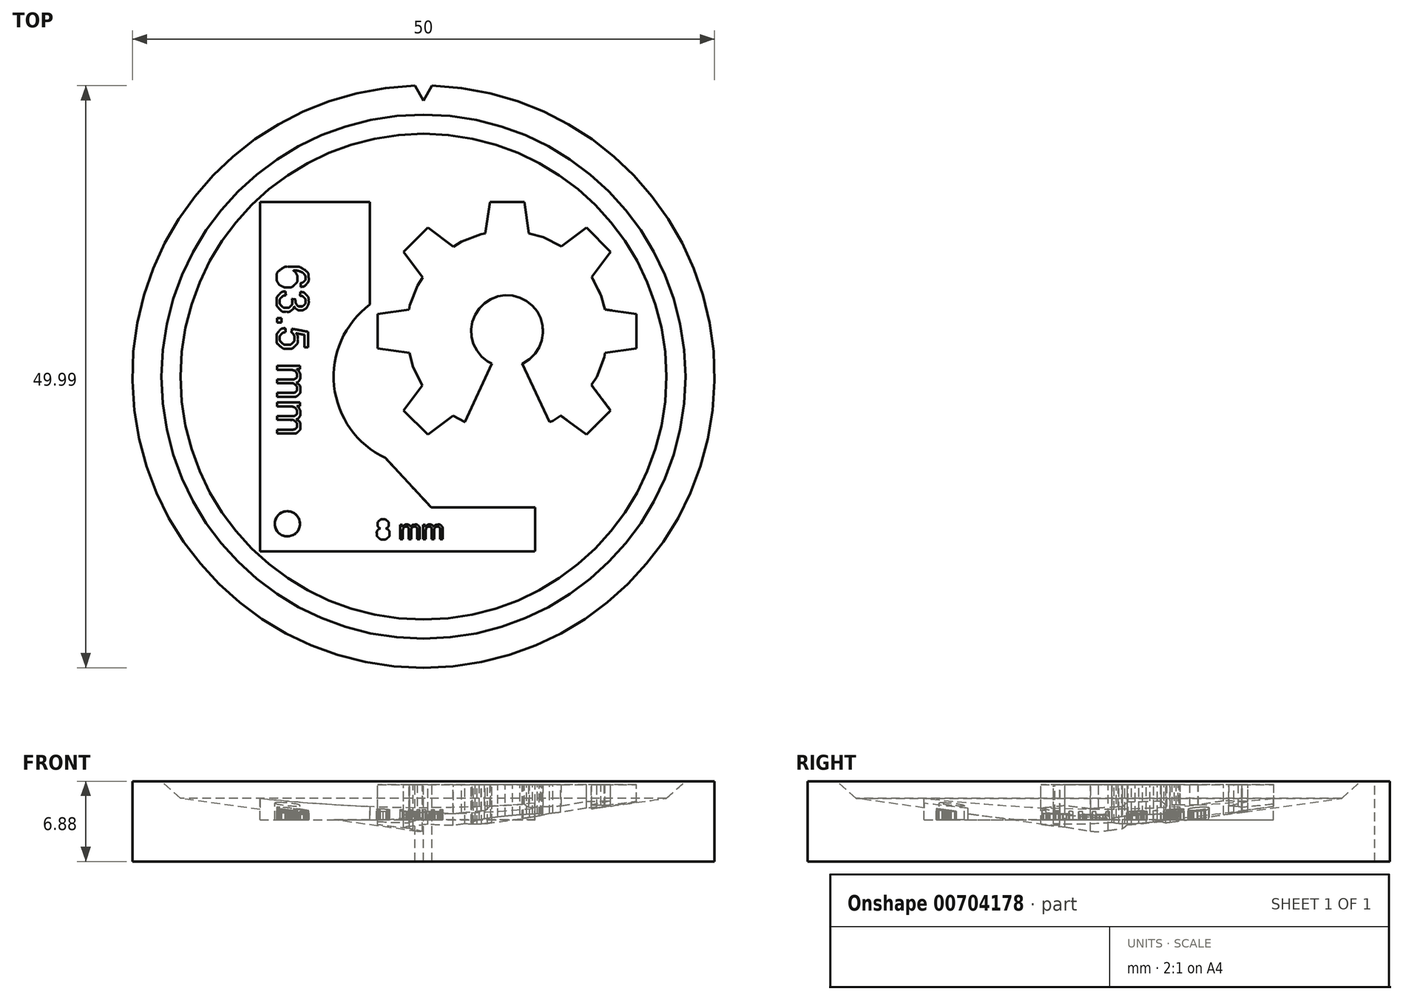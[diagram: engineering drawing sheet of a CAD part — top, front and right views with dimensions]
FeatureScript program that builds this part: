
annotation { "Feature Type Name" : "Feature", "Feature Type Description" : "" }
export const myFeature = defineFeature(function(context is Context, id is Id, definition is map)
    precondition{}
    {
        {
            var Q0;
            Q0=qCreatedBy(makeId("Front.planeOp"),FACE);
            var sketch = newSketch(context, id + "F0", { "sketchPlane" : qUnion([Q0])});
            skLineSegment(sketch, "E0", {"start": v(0, 0) * mm, "end": v(-25, 0) * mm});
            skLineSegment(sketch, "E1", {"start": v(-25, 0) * mm, "end": v(-25, 6.88) * mm});
            skLineSegment(sketch, "E2", {"start": v(-25, 6.88) * mm, "end": v(-22.5, 6.88) * mm});
            skLineSegment(sketch, "E3", {"start": v(-22.5, 6.88) * mm, "end": v(-20.86, 5.42) * mm});
            skLineSegment(sketch, "E4", {"start": v(-20.86, 5.42) * mm, "end": v(0, 2.5) * mm});
            skLineSegment(sketch, "E5", {"start": v(0, 2.5) * mm, "end": v(0, 0) * mm});
            skSolve(sketch);
        }
        {
            var Q0;
            Q0 = qSketchRegion(id + "F0", true);
            var Q1;
            Q1=sQuery(id+"F0.wireOp",EDGE,"E5");
            revolve(context, id + "F1", {"surfaceOperationType" : NewSurfaceOperationType.NEW, "entities" : qUnion([Q0]), "axis" : qUnion([Q1]), "revolveType" : RevolveType.FULL});
        }
        {
            var Q0;
            Q0=makeQuery(id+"F1.opRevolve","SWEPT_FACE",FACE,{"disambiguationData":[OSD([sQuery(id+"F0.wireOp",EDGE,"E2")])]});
            cPlane(context, id + "F2", {"entities" : qUnion([Q0]), "cplaneType" : CPlaneType.OFFSET, "offset" : 25 * mm, "width" : 150 * mm, "height" : 150 * mm});
        }
        {
            var Q0;
            Q0=qCreatedBy(id+"F2.planeOp",FACE);
            var sketch = newSketch(context, id + "F3", { "sketchPlane" : qUnion([Q0])});
            skCircle(sketch, "E6.cCircle", {"center": v(0, 25.35) * mm, "radius": 0.82 * mm, "construction": true});
            skLineSegment(sketch, "E6.0", {"start": v(-1.43, 26.17) * mm, "end": v(1.43, 26.17) * mm});
            skLineSegment(sketch, "E6.1", {"start": v(1.43, 26.17) * mm, "end": v(0, 23.7) * mm});
            skLineSegment(sketch, "E6.2", {"start": v(0, 23.7) * mm, "end": v(-1.43, 26.17) * mm});
            skPoint(sketch, "E6.0.midPoint", {"position": v(0, 26.17) * mm});
            skSolve(sketch);
        }
        {
            var Q0;
            Q0 = qSketchRegion(id + "F3", true);
            extrude(context, id + "F4", {"entities" : qUnion([Q0]), "operationType" : NewBodyOperationType.REMOVE, "oppositeDirection" : true, "depth" : 64 * mm, "offsetDistance" : 25 * mm});
        }
        {
            var Q0;
            Q0=qCreatedBy(id+"F2.planeOp",FACE);
            var sketch = newSketch(context, id + "F5", { "sketchPlane" : qUnion([Q0])});
            skLineSegment(sketch, "E7", {"start": v(-14.05, -15) * mm, "end": v(-14.05, 15) * mm});
            skLineSegment(sketch, "E8", {"start": v(-14.05, 15) * mm, "end": v(-4.6, 15) * mm});
            skLineSegment(sketch, "E9", {"start": v(-14.05, -15) * mm, "end": v(9.57, -15) * mm});
            skLineSegment(sketch, "E10", {"start": v(9.57, -15) * mm, "end": v(9.6, -11.22) * mm});
            skLineSegment(sketch, "E11", {"start": v(9.6, -11.22) * mm, "end": v(0.66, -11.22) * mm});
            skLineSegment(sketch, "E12", {"start": v(-4.6, -5.55) * mm, "end": v(-4.6, 15) * mm});
            skLineSegment(sketch, "E13", {"start": v(0.66, -11.22) * mm, "end": v(-4.6, -5.55) * mm});
            skCircle(sketch, "E14", {"center": v(-11.69, -12.64) * mm, "radius": 1.08 * mm});
            skLineSegment(sketch, "E15", {"start": v(-10.53, 7.7) * mm, "end": v(-10.56, 8.04) * mm});
            skLineSegment(sketch, "E16", {"start": v(-11.86, 7.33) * mm, "end": v(-11.81, 7) * mm});
            skLineSegment(sketch, "E17", {"start": v(-11.3, 6.67) * mm, "end": v(-11, 6.63) * mm});
            skLineSegment(sketch, "E18", {"start": v(-10.62, 6.96) * mm, "end": v(-10.56, 7.3) * mm});
            skLineSegment(sketch, "E19", {"start": v(-12.2, 5.04) * mm, "end": v(-12.57, 5.04) * mm});
            skLineSegment(sketch, "E20", {"start": v(-12.57, 5.04) * mm, "end": v(-12.57, 4.66) * mm});
            skLineSegment(sketch, "E21", {"start": v(-12.57, 4.66) * mm, "end": v(-12.2, 4.66) * mm});
            skLineSegment(sketch, "E22", {"start": v(-12.2, 4.66) * mm, "end": v(-12.2, 5.04) * mm});
            skLineSegment(sketch, "E23", {"start": v(-11.86, 4.17) * mm, "end": v(-11.83, 3.83) * mm});
            skLineSegment(sketch, "E24", {"start": v(-11.33, 3.8) * mm, "end": v(-11.3, 4.12) * mm});
            skLineSegment(sketch, "E25", {"start": v(-11.3, 4.12) * mm, "end": v(-9.9, 3.85) * mm});
            skLineSegment(sketch, "E26", {"start": v(-9.9, 3.85) * mm, "end": v(-9.9, 2.5) * mm});
            skLineSegment(sketch, "E27", {"start": v(-9.9, 2.5) * mm, "end": v(-10.22, 2.5) * mm});
            skLineSegment(sketch, "E28", {"start": v(-10.22, 2.5) * mm, "end": v(-10.22, 3.59) * mm});
            skLineSegment(sketch, "E29", {"start": v(-10.22, 3.59) * mm, "end": v(-10.95, 3.73) * mm});
            skLineSegment(sketch, "E30", {"start": v(-12.57, 0.93) * mm, "end": v(-10.61, 0.93) * mm});
            skLineSegment(sketch, "E31", {"start": v(-10.61, 0.93) * mm, "end": v(-10.61, 0.63) * mm});
            skLineSegment(sketch, "E32", {"start": v(-10.61, 0.63) * mm, "end": v(-10.89, 0.63) * mm});
            skLineSegment(sketch, "E33", {"start": v(-11.23, -1.73) * mm, "end": v(-12.57, -1.73) * mm});
            skLineSegment(sketch, "E34", {"start": v(-12.57, -1.73) * mm, "end": v(-12.57, -1.4) * mm});
            skLineSegment(sketch, "E35", {"start": v(-12.57, -1.4) * mm, "end": v(-11.34, -1.4) * mm});
            skLineSegment(sketch, "E36", {"start": v(-11.43, -0.57) * mm, "end": v(-12.57, -0.57) * mm});
            skLineSegment(sketch, "E37", {"start": v(-12.57, -0.57) * mm, "end": v(-12.57, -0.23) * mm});
            skLineSegment(sketch, "E38", {"start": v(-12.57, -0.23) * mm, "end": v(-11.3, -0.23) * mm});
            skLineSegment(sketch, "E39", {"start": v(-11.56, 0.6) * mm, "end": v(-12.57, 0.6) * mm});
            skLineSegment(sketch, "E40", {"start": v(-12.57, 0.6) * mm, "end": v(-12.57, 0.93) * mm});
            skLineSegment(sketch, "E41", {"start": v(-12.57, -2.22) * mm, "end": v(-10.61, -2.22) * mm});
            skLineSegment(sketch, "E42", {"start": v(-10.61, -2.22) * mm, "end": v(-10.61, -2.51) * mm});
            skLineSegment(sketch, "E43", {"start": v(-10.61, -2.51) * mm, "end": v(-10.89, -2.51) * mm});
            skLineSegment(sketch, "E44", {"start": v(-11.23, -4.87) * mm, "end": v(-12.57, -4.87) * mm});
            skLineSegment(sketch, "E45", {"start": v(-12.57, -4.87) * mm, "end": v(-12.57, -4.54) * mm});
            skLineSegment(sketch, "E46", {"start": v(-12.57, -4.54) * mm, "end": v(-11.34, -4.54) * mm});
            skLineSegment(sketch, "E47", {"start": v(-11.43, -3.71) * mm, "end": v(-12.57, -3.71) * mm});
            skLineSegment(sketch, "E48", {"start": v(-12.57, -3.71) * mm, "end": v(-12.57, -3.38) * mm});
            skLineSegment(sketch, "E49", {"start": v(-12.57, -3.38) * mm, "end": v(-11.3, -3.38) * mm});
            skLineSegment(sketch, "E50", {"start": v(-11.56, -2.55) * mm, "end": v(-12.57, -2.55) * mm});
            skLineSegment(sketch, "E51", {"start": v(-12.57, -2.55) * mm, "end": v(-12.57, -2.22) * mm});
            skFitSpline(sketch, "E52", {"points": [v(-10.56, 8.04) * mm, v(-10.5, 8.05) * mm, v(-10.4, 8.07) * mm, v(-10.3, 8.13) * mm, v(-10.27, 8.16) * mm]});
            skFitSpline(sketch, "E53", {"points": [v(-10.27, 8.16) * mm, v(-10.23, 8.2) * mm, v(-10.15, 8.3) * mm, v(-10.14, 8.43) * mm, v(-10.13, 8.5) * mm]});
            skFitSpline(sketch, "E54", {"points": [v(-10.13, 8.5) * mm, v(-10.13, 8.54) * mm, v(-10.14, 8.64) * mm, v(-10.2, 8.73) * mm, v(-10.22, 8.77) * mm]});
            skFitSpline(sketch, "E55", {"points": [v(-10.22, 8.77) * mm, v(-10.26, 8.82) * mm, v(-10.36, 8.93) * mm, v(-10.48, 8.99) * mm, v(-10.55, 9.02) * mm]});
            skFitSpline(sketch, "E56", {"points": [v(-10.55, 9.02) * mm, v(-10.64, 9.05) * mm, v(-10.84, 9.1) * mm, v(-11.06, 9.11) * mm, v(-11.18, 9.11) * mm]});
            skFitSpline(sketch, "E57", {"points": [v(-11.18, 9.11) * mm, v(-11.12, 9.07) * mm, v(-11.01, 9) * mm, v(-10.94, 8.88) * mm, v(-10.9, 8.82) * mm]});
            skFitSpline(sketch, "E58", {"points": [v(-10.9, 8.82) * mm, v(-10.88, 8.76) * mm, v(-10.83, 8.65) * mm, v(-10.82, 8.52) * mm, v(-10.82, 8.46) * mm]});
            skFitSpline(sketch, "E59", {"points": [v(-10.82, 8.46) * mm, v(-10.83, 8.35) * mm, v(-10.85, 8.13) * mm, v(-11, 7.97) * mm, v(-11.06, 7.9) * mm]});
            skFitSpline(sketch, "E60", {"points": [v(-11.06, 7.9) * mm, v(-11.15, 7.82) * mm, v(-11.34, 7.68) * mm, v(-11.57, 7.67) * mm, v(-11.7, 7.66) * mm]});
            skFitSpline(sketch, "E61", {"points": [v(-11.7, 7.66) * mm, v(-11.78, 7.66) * mm, v(-11.94, 7.67) * mm, v(-12.1, 7.74) * mm, v(-12.17, 7.77) * mm]});
            skFitSpline(sketch, "E62", {"points": [v(-12.17, 7.77) * mm, v(-12.24, 7.8) * mm, v(-12.37, 7.88) * mm, v(-12.46, 8) * mm, v(-12.5, 8.07) * mm]});
            skFitSpline(sketch, "E63", {"points": [v(-12.5, 8.07) * mm, v(-12.54, 8.14) * mm, v(-12.6, 8.27) * mm, v(-12.61, 8.43) * mm, v(-12.62, 8.5) * mm]});
            skFitSpline(sketch, "E64", {"points": [v(-12.62, 8.5) * mm, v(-12.6, 8.64) * mm, v(-12.58, 8.9) * mm, v(-12.4, 9.09) * mm, v(-12.31, 9.18) * mm]});
            skFitSpline(sketch, "E65", {"points": [v(-12.31, 9.18) * mm, v(-12.18, 9.26) * mm, v(-11.87, 9.44) * mm, v(-11.51, 9.44) * mm, v(-11.3, 9.44) * mm]});
            skFitSpline(sketch, "E66", {"points": [v(-11.3, 9.44) * mm, v(-11.08, 9.44) * mm, v(-10.67, 9.43) * mm, v(-10.32, 9.24) * mm, v(-10.17, 9.15) * mm]});
            skFitSpline(sketch, "E67", {"points": [v(-10.17, 9.15) * mm, v(-10.08, 9.06) * mm, v(-9.9, 8.87) * mm, v(-9.87, 8.6) * mm, v(-9.86, 8.47) * mm]});
            skFitSpline(sketch, "E68", {"points": [v(-9.86, 8.47) * mm, v(-9.86, 8.37) * mm, v(-9.87, 8.18) * mm, v(-9.98, 8.02) * mm, v(-10.04, 7.95) * mm]});
            skFitSpline(sketch, "E69", {"points": [v(-10.04, 7.95) * mm, v(-10.1, 7.89) * mm, v(-10.24, 7.76) * mm, v(-10.43, 7.72) * mm, v(-10.53, 7.7) * mm]});
            skFitSpline(sketch, "E70", {"points": [v(-11.7, 9.06) * mm, v(-11.75, 9.06) * mm, v(-11.87, 9.05) * mm, v(-11.97, 9.01) * mm, v(-12.02, 8.99) * mm]});
            skFitSpline(sketch, "E71", {"points": [v(-12.02, 8.99) * mm, v(-12.07, 8.96) * mm, v(-12.17, 8.91) * mm, v(-12.23, 8.83) * mm, v(-12.26, 8.78) * mm]});
            skFitSpline(sketch, "E72", {"points": [v(-12.26, 8.78) * mm, v(-12.29, 8.74) * mm, v(-12.33, 8.66) * mm, v(-12.34, 8.56) * mm, v(-12.35, 8.5) * mm]});
            skFitSpline(sketch, "E73", {"points": [v(-12.35, 8.5) * mm, v(-12.34, 8.44) * mm, v(-12.32, 8.3) * mm, v(-12.23, 8.2) * mm, v(-12.18, 8.15) * mm]});
            skFitSpline(sketch, "E74", {"points": [v(-12.18, 8.15) * mm, v(-12.11, 8.1) * mm, v(-11.97, 8) * mm, v(-11.8, 8) * mm, v(-11.71, 8) * mm]});
            skFitSpline(sketch, "E75", {"points": [v(-11.71, 8) * mm, v(-11.63, 8) * mm, v(-11.47, 8) * mm, v(-11.33, 8.1) * mm, v(-11.27, 8.15) * mm]});
            skFitSpline(sketch, "E76", {"points": [v(-11.27, 8.15) * mm, v(-11.23, 8.2) * mm, v(-11.13, 8.3) * mm, v(-11.12, 8.45) * mm, v(-11.11, 8.52) * mm]});
            skFitSpline(sketch, "E77", {"points": [v(-11.11, 8.52) * mm, v(-11.12, 8.6) * mm, v(-11.13, 8.74) * mm, v(-11.23, 8.85) * mm, v(-11.27, 8.9) * mm]});
            skFitSpline(sketch, "E78", {"points": [v(-11.27, 8.9) * mm, v(-11.33, 8.95) * mm, v(-11.46, 9.05) * mm, v(-11.61, 9.06) * mm, v(-11.7, 9.06) * mm]});
            skFitSpline(sketch, "E79", {"points": [v(-11.81, 7) * mm, v(-11.9, 6.97) * mm, v(-12.05, 6.94) * mm, v(-12.17, 6.84) * mm, v(-12.22, 6.8) * mm]});
            skFitSpline(sketch, "E80", {"points": [v(-12.22, 6.8) * mm, v(-12.26, 6.75) * mm, v(-12.33, 6.65) * mm, v(-12.34, 6.53) * mm, v(-12.35, 6.46) * mm]});
            skFitSpline(sketch, "E81", {"points": [v(-12.35, 6.46) * mm, v(-12.34, 6.39) * mm, v(-12.33, 6.24) * mm, v(-12.23, 6.12) * mm, v(-12.18, 6.07) * mm]});
            skFitSpline(sketch, "E82", {"points": [v(-12.18, 6.07) * mm, v(-12.13, 6.02) * mm, v(-12, 5.92) * mm, v(-11.86, 5.91) * mm, v(-11.78, 5.9) * mm]});
            skFitSpline(sketch, "E83", {"points": [v(-11.78, 5.9) * mm, v(-11.7, 5.91) * mm, v(-11.57, 5.92) * mm, v(-11.46, 6.01) * mm, v(-11.4, 6.06) * mm]});
            skFitSpline(sketch, "E84", {"points": [v(-11.4, 6.06) * mm, v(-11.36, 6.1) * mm, v(-11.27, 6.22) * mm, v(-11.26, 6.36) * mm, v(-11.26, 6.44) * mm]});
            skFitSpline(sketch, "E85", {"points": [v(-11.26, 6.44) * mm, v(-11.26, 6.47) * mm, v(-11.26, 6.55) * mm, v(-11.28, 6.63) * mm, v(-11.3, 6.67) * mm]});
            skFitSpline(sketch, "E86", {"points": [v(-11, 6.63) * mm, v(-11, 6.62) * mm, v(-11, 6.6) * mm, v(-11, 6.59) * mm, v(-11, 6.58) * mm]});
            skFitSpline(sketch, "E87", {"points": [v(-11, 6.58) * mm, v(-11, 6.51) * mm, v(-11, 6.38) * mm, v(-10.93, 6.26) * mm, v(-10.9, 6.2) * mm]});
            skFitSpline(sketch, "E88", {"points": [v(-10.9, 6.2) * mm, v(-10.85, 6.15) * mm, v(-10.76, 6.05) * mm, v(-10.62, 6.03) * mm, v(-10.55, 6.03) * mm]});
            skFitSpline(sketch, "E89", {"points": [v(-10.55, 6.03) * mm, v(-10.5, 6.03) * mm, v(-10.38, 6.04) * mm, v(-10.3, 6.12) * mm, v(-10.25, 6.15) * mm]});
            skFitSpline(sketch, "E90", {"points": [v(-10.25, 6.15) * mm, v(-10.21, 6.2) * mm, v(-10.14, 6.3) * mm, v(-10.13, 6.4) * mm, v(-10.13, 6.47) * mm]});
            skFitSpline(sketch, "E91", {"points": [v(-10.13, 6.47) * mm, v(-10.13, 6.53) * mm, v(-10.14, 6.65) * mm, v(-10.22, 6.75) * mm, v(-10.25, 6.8) * mm]});
            skFitSpline(sketch, "E92", {"points": [v(-10.25, 6.8) * mm, v(-10.3, 6.83) * mm, v(-10.4, 6.92) * mm, v(-10.54, 6.95) * mm, v(-10.62, 6.96) * mm]});
            skFitSpline(sketch, "E93", {"points": [v(-10.56, 7.3) * mm, v(-10.45, 7.27) * mm, v(-10.26, 7.22) * mm, v(-10.1, 7.08) * mm, v(-10.04, 7.02) * mm]});
            skFitSpline(sketch, "E94", {"points": [v(-10.04, 7.02) * mm, v(-9.99, 6.94) * mm, v(-9.88, 6.78) * mm, v(-9.86, 6.58) * mm, v(-9.86, 6.48) * mm]});
            skFitSpline(sketch, "E95", {"points": [v(-9.86, 6.48) * mm, v(-9.86, 6.4) * mm, v(-9.87, 6.26) * mm, v(-9.92, 6.13) * mm, v(-9.95, 6.07) * mm]});
            skFitSpline(sketch, "E96", {"points": [v(-9.95, 6.07) * mm, v(-9.99, 6.01) * mm, v(-10.05, 5.9) * mm, v(-10.16, 5.82) * mm, v(-10.21, 5.79) * mm]});
            skFitSpline(sketch, "E97", {"points": [v(-10.21, 5.79) * mm, v(-10.27, 5.76) * mm, v(-10.38, 5.7) * mm, v(-10.5, 5.7) * mm, v(-10.56, 5.69) * mm]});
            skFitSpline(sketch, "E98", {"points": [v(-10.56, 5.69) * mm, v(-10.62, 5.7) * mm, v(-10.73, 5.7) * mm, v(-10.83, 5.75) * mm, v(-10.88, 5.78) * mm]});
            skFitSpline(sketch, "E99", {"points": [v(-10.88, 5.78) * mm, v(-10.92, 5.82) * mm, v(-11.02, 5.9) * mm, v(-11.08, 6) * mm, v(-11.1, 6.06) * mm]});
            skFitSpline(sketch, "E100", {"points": [v(-11.1, 6.06) * mm, v(-11.13, 5.98) * mm, v(-11.17, 5.84) * mm, v(-11.28, 5.74) * mm, v(-11.34, 5.69) * mm]});
            skFitSpline(sketch, "E101", {"points": [v(-11.34, 5.69) * mm, v(-11.4, 5.65) * mm, v(-11.53, 5.57) * mm, v(-11.7, 5.56) * mm, v(-11.77, 5.55) * mm]});
            skFitSpline(sketch, "E102", {"points": [v(-11.77, 5.55) * mm, v(-11.89, 5.56) * mm, v(-12.12, 5.59) * mm, v(-12.29, 5.74) * mm, v(-12.37, 5.81) * mm]});
            skFitSpline(sketch, "E103", {"points": [v(-12.37, 5.81) * mm, v(-12.45, 5.9) * mm, v(-12.6, 6.1) * mm, v(-12.61, 6.34) * mm, v(-12.62, 6.47) * mm]});
            skFitSpline(sketch, "E104", {"points": [v(-12.62, 6.47) * mm, v(-12.61, 6.58) * mm, v(-12.6, 6.8) * mm, v(-12.47, 6.97) * mm, v(-12.4, 7.06) * mm]});
            skFitSpline(sketch, "E105", {"points": [v(-12.4, 7.06) * mm, v(-12.33, 7.13) * mm, v(-12.17, 7.27) * mm, v(-11.97, 7.3) * mm, v(-11.86, 7.33) * mm]});
            skFitSpline(sketch, "E106", {"points": [v(-11.83, 3.83) * mm, v(-11.91, 3.81) * mm, v(-12.06, 3.78) * mm, v(-12.17, 3.69) * mm, v(-12.22, 3.65) * mm]});
            skFitSpline(sketch, "E107", {"points": [v(-12.22, 3.65) * mm, v(-12.25, 3.6) * mm, v(-12.33, 3.5) * mm, v(-12.34, 3.37) * mm, v(-12.35, 3.3) * mm]});
            skFitSpline(sketch, "E108", {"points": [v(-12.35, 3.3) * mm, v(-12.34, 3.23) * mm, v(-12.32, 3.07) * mm, v(-12.22, 2.96) * mm, v(-12.16, 2.9) * mm]});
            skFitSpline(sketch, "E109", {"points": [v(-12.16, 2.9) * mm, v(-12.1, 2.85) * mm, v(-11.95, 2.75) * mm, v(-11.78, 2.74) * mm, v(-11.69, 2.73) * mm]});
            skFitSpline(sketch, "E110", {"points": [v(-11.69, 2.73) * mm, v(-11.6, 2.74) * mm, v(-11.43, 2.75) * mm, v(-11.3, 2.85) * mm, v(-11.24, 2.9) * mm]});
            skFitSpline(sketch, "E111", {"points": [v(-11.24, 2.9) * mm, v(-11.19, 2.95) * mm, v(-11.09, 3.07) * mm, v(-11.08, 3.23) * mm, v(-11.07, 3.31) * mm]});
            skFitSpline(sketch, "E112", {"points": [v(-11.07, 3.31) * mm, v(-11.08, 3.36) * mm, v(-11.08, 3.46) * mm, v(-11.12, 3.56) * mm, v(-11.15, 3.6) * mm]});
            skFitSpline(sketch, "E113", {"points": [v(-11.15, 3.6) * mm, v(-11.17, 3.64) * mm, v(-11.22, 3.72) * mm, v(-11.3, 3.78) * mm, v(-11.33, 3.8) * mm]});
            skFitSpline(sketch, "E114", {"points": [v(-10.95, 3.73) * mm, v(-10.9, 3.65) * mm, v(-10.8, 3.5) * mm, v(-10.79, 3.31) * mm, v(-10.78, 3.22) * mm]});
            skFitSpline(sketch, "E115", {"points": [v(-10.78, 3.22) * mm, v(-10.79, 3.1) * mm, v(-10.8, 2.88) * mm, v(-10.95, 2.71) * mm, v(-11.02, 2.62) * mm]});
            skFitSpline(sketch, "E116", {"points": [v(-11.02, 2.62) * mm, v(-11.11, 2.55) * mm, v(-11.3, 2.4) * mm, v(-11.53, 2.39) * mm, v(-11.66, 2.38) * mm]});
            skFitSpline(sketch, "E117", {"points": [v(-11.66, 2.38) * mm, v(-11.77, 2.39) * mm, v(-12, 2.4) * mm, v(-12.2, 2.53) * mm, v(-12.3, 2.6) * mm]});
            skFitSpline(sketch, "E118", {"points": [v(-12.3, 2.6) * mm, v(-12.39, 2.7) * mm, v(-12.58, 2.89) * mm, v(-12.6, 3.16) * mm, v(-12.62, 3.3) * mm]});
            skFitSpline(sketch, "E119", {"points": [v(-12.62, 3.3) * mm, v(-12.61, 3.42) * mm, v(-12.6, 3.64) * mm, v(-12.47, 3.82) * mm, v(-12.41, 3.9) * mm]});
            skFitSpline(sketch, "E120", {"points": [v(-12.41, 3.9) * mm, v(-12.34, 3.98) * mm, v(-12.18, 4.12) * mm, v(-11.97, 4.16) * mm, v(-11.86, 4.17) * mm]});
            skFitSpline(sketch, "E121", {"points": [v(-10.89, 0.63) * mm, v(-10.84, 0.6) * mm, v(-10.75, 0.53) * mm, v(-10.69, 0.44) * mm, v(-10.66, 0.39) * mm]});
            skFitSpline(sketch, "E122", {"points": [v(-10.66, 0.39) * mm, v(-10.63, 0.33) * mm, v(-10.58, 0.22) * mm, v(-10.57, 0.1) * mm, v(-10.57, 0.04) * mm]});
            skFitSpline(sketch, "E123", {"points": [v(-10.57, 0.04) * mm, v(-10.57, -0.03) * mm, v(-10.58, -0.15) * mm, v(-10.63, -0.27) * mm, v(-10.66, -0.32) * mm]});
            skFitSpline(sketch, "E124", {"points": [v(-10.66, -0.32) * mm, v(-10.7, -0.36) * mm, v(-10.76, -0.45) * mm, v(-10.86, -0.5) * mm, v(-10.91, -0.51) * mm]});
            skFitSpline(sketch, "E125", {"points": [v(-10.91, -0.51) * mm, v(-10.81, -0.6) * mm, v(-10.62, -0.75) * mm, v(-10.58, -1) * mm, v(-10.57, -1.12) * mm]});
            skFitSpline(sketch, "E126", {"points": [v(-10.57, -1.12) * mm, v(-10.57, -1.2) * mm, v(-10.58, -1.38) * mm, v(-10.68, -1.5) * mm, v(-10.73, -1.57) * mm]});
            skFitSpline(sketch, "E127", {"points": [v(-10.73, -1.57) * mm, v(-10.8, -1.61) * mm, v(-10.94, -1.72) * mm, v(-11.13, -1.72) * mm, v(-11.23, -1.73) * mm]});
            skFitSpline(sketch, "E128", {"points": [v(-11.34, -1.4) * mm, v(-11.28, -1.4) * mm, v(-11.18, -1.4) * mm, v(-11.09, -1.37) * mm, v(-11.05, -1.36) * mm]});
            skFitSpline(sketch, "E129", {"points": [v(-11.05, -1.36) * mm, v(-11.02, -1.35) * mm, v(-10.97, -1.32) * mm, v(-10.93, -1.27) * mm, v(-10.9, -1.25) * mm]});
            skFitSpline(sketch, "E130", {"points": [v(-10.9, -1.25) * mm, v(-10.9, -1.22) * mm, v(-10.86, -1.15) * mm, v(-10.86, -1.08) * mm, v(-10.86, -1.05) * mm]});
            skFitSpline(sketch, "E131", {"points": [v(-10.86, -1.05) * mm, v(-10.86, -0.98) * mm, v(-10.87, -0.85) * mm, v(-10.95, -0.75) * mm, v(-11, -0.7) * mm]});
            skFitSpline(sketch, "E132", {"points": [v(-11, -0.7) * mm, v(-11.05, -0.66) * mm, v(-11.18, -0.57) * mm, v(-11.34, -0.57) * mm, v(-11.43, -0.57) * mm]});
            skFitSpline(sketch, "E133", {"points": [v(-11.3, -0.23) * mm, v(-11.23, -0.23) * mm, v(-11.12, -0.23) * mm, v(-11.01, -0.18) * mm, v(-10.97, -0.15) * mm]});
            skFitSpline(sketch, "E134", {"points": [v(-10.97, -0.15) * mm, v(-10.93, -0.12) * mm, v(-10.86, -0.05) * mm, v(-10.86, 0.06) * mm, v(-10.86, 0.11) * mm]});
            skFitSpline(sketch, "E135", {"points": [v(-10.86, 0.11) * mm, v(-10.86, 0.16) * mm, v(-10.87, 0.25) * mm, v(-10.9, 0.33) * mm, v(-10.93, 0.37) * mm]});
            skFitSpline(sketch, "E136", {"points": [v(-10.93, 0.37) * mm, v(-10.96, 0.4) * mm, v(-11.02, 0.49) * mm, v(-11.1, 0.52) * mm, v(-11.15, 0.54) * mm]});
            skFitSpline(sketch, "E137", {"points": [v(-11.15, 0.54) * mm, v(-11.2, 0.56) * mm, v(-11.34, 0.6) * mm, v(-11.48, 0.6) * mm, v(-11.56, 0.6) * mm]});
            skFitSpline(sketch, "E138", {"points": [v(-10.89, -2.51) * mm, v(-10.84, -2.55) * mm, v(-10.75, -2.62) * mm, v(-10.69, -2.71) * mm, v(-10.66, -2.76) * mm]});
            skFitSpline(sketch, "E139", {"points": [v(-10.66, -2.76) * mm, v(-10.63, -2.81) * mm, v(-10.58, -2.92) * mm, v(-10.57, -3.05) * mm, v(-10.57, -3.1) * mm]});
            skFitSpline(sketch, "E140", {"points": [v(-10.57, -3.1) * mm, v(-10.57, -3.18) * mm, v(-10.58, -3.3) * mm, v(-10.63, -3.41) * mm, v(-10.66, -3.47) * mm]});
            skFitSpline(sketch, "E141", {"points": [v(-10.66, -3.47) * mm, v(-10.7, -3.5) * mm, v(-10.76, -3.6) * mm, v(-10.86, -3.64) * mm, v(-10.91, -3.66) * mm]});
            skFitSpline(sketch, "E142", {"points": [v(-10.91, -3.66) * mm, v(-10.81, -3.74) * mm, v(-10.62, -3.9) * mm, v(-10.58, -4.15) * mm, v(-10.57, -4.27) * mm]});
            skFitSpline(sketch, "E143", {"points": [v(-10.57, -4.27) * mm, v(-10.57, -4.36) * mm, v(-10.58, -4.52) * mm, v(-10.68, -4.66) * mm, v(-10.73, -4.72) * mm]});
            skFitSpline(sketch, "E144", {"points": [v(-10.73, -4.72) * mm, v(-10.8, -4.76) * mm, v(-10.94, -4.86) * mm, v(-11.13, -4.87) * mm, v(-11.23, -4.87) * mm]});
            skFitSpline(sketch, "E145", {"points": [v(-11.34, -4.54) * mm, v(-11.28, -4.54) * mm, v(-11.18, -4.54) * mm, v(-11.09, -4.52) * mm, v(-11.05, -4.51) * mm]});
            skFitSpline(sketch, "E146", {"points": [v(-11.05, -4.51) * mm, v(-11.02, -4.5) * mm, v(-10.97, -4.47) * mm, v(-10.93, -4.42) * mm, v(-10.9, -4.4) * mm]});
            skFitSpline(sketch, "E147", {"points": [v(-10.9, -4.4) * mm, v(-10.9, -4.36) * mm, v(-10.86, -4.3) * mm, v(-10.86, -4.23) * mm, v(-10.86, -4.2) * mm]});
            skFitSpline(sketch, "E148", {"points": [v(-10.86, -4.2) * mm, v(-10.86, -4.13) * mm, v(-10.87, -4) * mm, v(-10.95, -3.9) * mm, v(-11, -3.85) * mm]});
            skFitSpline(sketch, "E149", {"points": [v(-11, -3.85) * mm, v(-11.05, -3.81) * mm, v(-11.18, -3.72) * mm, v(-11.34, -3.72) * mm, v(-11.43, -3.71) * mm]});
            skFitSpline(sketch, "E150", {"points": [v(-11.3, -3.38) * mm, v(-11.23, -3.38) * mm, v(-11.12, -3.38) * mm, v(-11.01, -3.32) * mm, v(-10.97, -3.3) * mm]});
            skFitSpline(sketch, "E151", {"points": [v(-10.97, -3.3) * mm, v(-10.93, -3.27) * mm, v(-10.86, -3.2) * mm, v(-10.86, -3.1) * mm, v(-10.86, -3.04) * mm]});
            skFitSpline(sketch, "E152", {"points": [v(-10.86, -3.04) * mm, v(-10.86, -2.99) * mm, v(-10.87, -2.9) * mm, v(-10.9, -2.82) * mm, v(-10.93, -2.78) * mm]});
            skFitSpline(sketch, "E153", {"points": [v(-10.93, -2.78) * mm, v(-10.96, -2.74) * mm, v(-11.02, -2.66) * mm, v(-11.1, -2.62) * mm, v(-11.15, -2.6) * mm]});
            skFitSpline(sketch, "E154", {"points": [v(-11.15, -2.6) * mm, v(-11.2, -2.59) * mm, v(-11.34, -2.55) * mm, v(-11.48, -2.55) * mm, v(-11.56, -2.55) * mm]});
            skLineSegment(sketch, "E155", {"start": v(-1.99, -13.95) * mm, "end": v(-1.99, -12.72) * mm});
            skLineSegment(sketch, "E156", {"start": v(-1.99, -12.72) * mm, "end": v(-1.8, -12.72) * mm});
            skLineSegment(sketch, "E157", {"start": v(-1.8, -12.72) * mm, "end": v(-1.8, -12.9) * mm});
            skLineSegment(sketch, "E158", {"start": v(-0.33, -13.1) * mm, "end": v(-0.33, -13.95) * mm});
            skLineSegment(sketch, "E159", {"start": v(-0.33, -13.95) * mm, "end": v(-0.54, -13.95) * mm});
            skLineSegment(sketch, "E160", {"start": v(-0.54, -13.95) * mm, "end": v(-0.54, -13.18) * mm});
            skLineSegment(sketch, "E161", {"start": v(-1.05, -13.24) * mm, "end": v(-1.05, -13.95) * mm});
            skLineSegment(sketch, "E162", {"start": v(-1.05, -13.95) * mm, "end": v(-1.26, -13.95) * mm});
            skLineSegment(sketch, "E163", {"start": v(-1.26, -13.95) * mm, "end": v(-1.26, -13.15) * mm});
            skLineSegment(sketch, "E164", {"start": v(-1.78, -13.31) * mm, "end": v(-1.78, -13.95) * mm});
            skLineSegment(sketch, "E165", {"start": v(-1.78, -13.95) * mm, "end": v(-1.99, -13.95) * mm});
            skLineSegment(sketch, "E166", {"start": v(-0.02, -13.95) * mm, "end": v(-0.02, -12.72) * mm});
            skLineSegment(sketch, "E167", {"start": v(-0.02, -12.72) * mm, "end": v(0.16, -12.72) * mm});
            skLineSegment(sketch, "E168", {"start": v(0.16, -12.72) * mm, "end": v(0.16, -12.9) * mm});
            skLineSegment(sketch, "E169", {"start": v(1.64, -13.1) * mm, "end": v(1.64, -13.95) * mm});
            skLineSegment(sketch, "E170", {"start": v(1.64, -13.95) * mm, "end": v(1.43, -13.95) * mm});
            skLineSegment(sketch, "E171", {"start": v(1.43, -13.95) * mm, "end": v(1.43, -13.18) * mm});
            skLineSegment(sketch, "E172", {"start": v(0.91, -13.24) * mm, "end": v(0.91, -13.95) * mm});
            skLineSegment(sketch, "E173", {"start": v(0.91, -13.95) * mm, "end": v(0.7, -13.95) * mm});
            skLineSegment(sketch, "E174", {"start": v(0.7, -13.95) * mm, "end": v(0.7, -13.15) * mm});
            skLineSegment(sketch, "E175", {"start": v(0.19, -13.31) * mm, "end": v(0.19, -13.95) * mm});
            skLineSegment(sketch, "E176", {"start": v(0.19, -13.95) * mm, "end": v(-0.02, -13.95) * mm});
            skFitSpline(sketch, "E177", {"points": [v(-3.7, -13.03) * mm, v(-3.74, -13.02) * mm, v(-3.81, -12.99) * mm, v(-3.86, -12.93) * mm, v(-3.89, -12.9) * mm]});
            skFitSpline(sketch, "E178", {"points": [v(-3.89, -12.9) * mm, v(-3.9, -12.87) * mm, v(-3.94, -12.8) * mm, v(-3.95, -12.73) * mm, v(-3.95, -12.69) * mm]});
            skFitSpline(sketch, "E179", {"points": [v(-3.95, -12.69) * mm, v(-3.94, -12.63) * mm, v(-3.93, -12.51) * mm, v(-3.86, -12.42) * mm, v(-3.82, -12.38) * mm]});
            skFitSpline(sketch, "E180", {"points": [v(-3.82, -12.38) * mm, v(-3.77, -12.34) * mm, v(-3.66, -12.26) * mm, v(-3.53, -12.26) * mm, v(-3.46, -12.25) * mm]});
            skFitSpline(sketch, "E181", {"points": [v(-3.46, -12.25) * mm, v(-3.4, -12.26) * mm, v(-3.26, -12.26) * mm, v(-3.16, -12.34) * mm, v(-3.1, -12.38) * mm]});
            skFitSpline(sketch, "E182", {"points": [v(-3.1, -12.38) * mm, v(-3.07, -12.43) * mm, v(-3, -12.52) * mm, v(-2.98, -12.63) * mm, v(-2.97, -12.7) * mm]});
            skFitSpline(sketch, "E183", {"points": [v(-2.97, -12.7) * mm, v(-2.98, -12.73) * mm, v(-2.98, -12.8) * mm, v(-3.02, -12.87) * mm, v(-3.04, -12.9) * mm]});
            skFitSpline(sketch, "E184", {"points": [v(-3.04, -12.9) * mm, v(-3.06, -12.93) * mm, v(-3.11, -12.99) * mm, v(-3.18, -13.02) * mm, v(-3.22, -13.03) * mm]});
            skFitSpline(sketch, "E185", {"points": [v(-3.22, -13.03) * mm, v(-3.17, -13.05) * mm, v(-3.08, -13.09) * mm, v(-3.02, -13.16) * mm, v(-2.99, -13.2) * mm]});
            skFitSpline(sketch, "E186", {"points": [v(-2.99, -13.2) * mm, v(-2.96, -13.24) * mm, v(-2.91, -13.32) * mm, v(-2.9, -13.42) * mm, v(-2.9, -13.47) * mm]});
            skFitSpline(sketch, "E187", {"points": [v(-2.9, -13.47) * mm, v(-2.91, -13.54) * mm, v(-2.92, -13.67) * mm, v(-3.01, -13.78) * mm, v(-3.06, -13.83) * mm]});
            skFitSpline(sketch, "E188", {"points": [v(-3.06, -13.83) * mm, v(-3.11, -13.87) * mm, v(-3.23, -13.96) * mm, v(-3.38, -13.97) * mm, v(-3.46, -13.98) * mm]});
            skFitSpline(sketch, "E189", {"points": [v(-3.46, -13.98) * mm, v(-3.54, -13.97) * mm, v(-3.69, -13.96) * mm, v(-3.8, -13.87) * mm, v(-3.87, -13.83) * mm]});
            skFitSpline(sketch, "E190", {"points": [v(-3.87, -13.83) * mm, v(-3.9, -13.78) * mm, v(-4, -13.67) * mm, v(-4.01, -13.53) * mm, v(-4.02, -13.46) * mm]});
            skFitSpline(sketch, "E191", {"points": [v(-4.02, -13.46) * mm, v(-4.02, -13.4) * mm, v(-4.01, -13.3) * mm, v(-3.96, -13.22) * mm, v(-3.93, -13.18) * mm]});
            skFitSpline(sketch, "E192", {"points": [v(-3.93, -13.18) * mm, v(-3.9, -13.15) * mm, v(-3.84, -13.08) * mm, v(-3.74, -13.05) * mm, v(-3.7, -13.03) * mm]});
            skFitSpline(sketch, "E193", {"points": [v(-3.74, -12.68) * mm, v(-3.74, -12.72) * mm, v(-3.73, -12.8) * mm, v(-3.68, -12.85) * mm, v(-3.66, -12.88) * mm]});
            skFitSpline(sketch, "E194", {"points": [v(-3.66, -12.88) * mm, v(-3.63, -12.9) * mm, v(-3.57, -12.95) * mm, v(-3.5, -12.95) * mm, v(-3.46, -12.95) * mm]});
            skFitSpline(sketch, "E195", {"points": [v(-3.46, -12.95) * mm, v(-3.42, -12.95) * mm, v(-3.35, -12.95) * mm, v(-3.3, -12.9) * mm, v(-3.26, -12.88) * mm]});
            skFitSpline(sketch, "E196", {"points": [v(-3.26, -12.88) * mm, v(-3.24, -12.85) * mm, v(-3.2, -12.8) * mm, v(-3.2, -12.73) * mm, v(-3.19, -12.7) * mm]});
            skFitSpline(sketch, "E197", {"points": [v(-3.19, -12.7) * mm, v(-3.2, -12.66) * mm, v(-3.2, -12.58) * mm, v(-3.24, -12.53) * mm, v(-3.27, -12.5) * mm]});
            skFitSpline(sketch, "E198", {"points": [v(-3.27, -12.5) * mm, v(-3.3, -12.48) * mm, v(-3.35, -12.43) * mm, v(-3.43, -12.43) * mm, v(-3.46, -12.42) * mm]});
            skFitSpline(sketch, "E199", {"points": [v(-3.46, -12.42) * mm, v(-3.5, -12.43) * mm, v(-3.57, -12.43) * mm, v(-3.63, -12.48) * mm, v(-3.66, -12.5) * mm]});
            skFitSpline(sketch, "E200", {"points": [v(-3.66, -12.5) * mm, v(-3.68, -12.53) * mm, v(-3.73, -12.58) * mm, v(-3.73, -12.65) * mm, v(-3.74, -12.68) * mm]});
            skFitSpline(sketch, "E201", {"points": [v(-3.8, -13.46) * mm, v(-3.8, -13.5) * mm, v(-3.8, -13.55) * mm, v(-3.78, -13.6) * mm, v(-3.76, -13.63) * mm]});
            skFitSpline(sketch, "E202", {"points": [v(-3.76, -13.63) * mm, v(-3.75, -13.66) * mm, v(-3.72, -13.71) * mm, v(-3.66, -13.75) * mm, v(-3.64, -13.76) * mm]});
            skFitSpline(sketch, "E203", {"points": [v(-3.64, -13.76) * mm, v(-3.6, -13.78) * mm, v(-3.55, -13.8) * mm, v(-3.5, -13.8) * mm, v(-3.46, -13.8) * mm]});
            skFitSpline(sketch, "E204", {"points": [v(-3.46, -13.8) * mm, v(-3.41, -13.8) * mm, v(-3.32, -13.8) * mm, v(-3.25, -13.74) * mm, v(-3.21, -13.71) * mm]});
            skFitSpline(sketch, "E205", {"points": [v(-3.21, -13.71) * mm, v(-3.19, -13.68) * mm, v(-3.13, -13.6) * mm, v(-3.12, -13.52) * mm, v(-3.12, -13.47) * mm]});
            skFitSpline(sketch, "E206", {"points": [v(-3.12, -13.47) * mm, v(-3.12, -13.42) * mm, v(-3.13, -13.33) * mm, v(-3.19, -13.26) * mm, v(-3.22, -13.22) * mm]});
            skFitSpline(sketch, "E207", {"points": [v(-3.22, -13.22) * mm, v(-3.25, -13.2) * mm, v(-3.33, -13.13) * mm, v(-3.42, -13.13) * mm, v(-3.47, -13.12) * mm]});
            skFitSpline(sketch, "E208", {"points": [v(-3.47, -13.12) * mm, v(-3.51, -13.13) * mm, v(-3.6, -13.13) * mm, v(-3.67, -13.2) * mm, v(-3.7, -13.22) * mm]});
            skFitSpline(sketch, "E209", {"points": [v(-3.7, -13.22) * mm, v(-3.74, -13.25) * mm, v(-3.8, -13.33) * mm, v(-3.8, -13.42) * mm, v(-3.8, -13.46) * mm]});
            skFitSpline(sketch, "E210", {"points": [v(-1.8, -12.9) * mm, v(-1.78, -12.87) * mm, v(-1.74, -12.81) * mm, v(-1.68, -12.77) * mm, v(-1.65, -12.75) * mm]});
            skFitSpline(sketch, "E211", {"points": [v(-1.65, -12.75) * mm, v(-1.62, -12.74) * mm, v(-1.55, -12.7) * mm, v(-1.47, -12.7) * mm, v(-1.43, -12.7) * mm]});
            skFitSpline(sketch, "E212", {"points": [v(-1.43, -12.7) * mm, v(-1.39, -12.7) * mm, v(-1.31, -12.7) * mm, v(-1.24, -12.74) * mm, v(-1.2, -12.75) * mm]});
            skFitSpline(sketch, "E213", {"points": [v(-1.2, -12.75) * mm, v(-1.18, -12.77) * mm, v(-1.13, -12.82) * mm, v(-1.1, -12.88) * mm, v(-1.09, -12.91) * mm]});
            skFitSpline(sketch, "E214", {"points": [v(-1.09, -12.91) * mm, v(-1.03, -12.85) * mm, v(-0.94, -12.73) * mm, v(-0.78, -12.7) * mm, v(-0.7, -12.7) * mm]});
            skFitSpline(sketch, "E215", {"points": [v(-0.7, -12.7) * mm, v(-0.65, -12.7) * mm, v(-0.55, -12.7) * mm, v(-0.46, -12.77) * mm, v(-0.43, -12.8) * mm]});
            skFitSpline(sketch, "E216", {"points": [v(-0.43, -12.8) * mm, v(-0.4, -12.84) * mm, v(-0.33, -12.93) * mm, v(-0.33, -13.05) * mm, v(-0.33, -13.1) * mm]});
            skFitSpline(sketch, "E217", {"points": [v(-0.54, -13.18) * mm, v(-0.54, -13.14) * mm, v(-0.54, -13.08) * mm, v(-0.55, -13.02) * mm, v(-0.56, -13) * mm]});
            skFitSpline(sketch, "E218", {"points": [v(-0.56, -13) * mm, v(-0.56, -12.98) * mm, v(-0.58, -12.95) * mm, v(-0.61, -12.92) * mm, v(-0.63, -12.91) * mm]});
            skFitSpline(sketch, "E219", {"points": [v(-0.63, -12.91) * mm, v(-0.65, -12.9) * mm, v(-0.69, -12.88) * mm, v(-0.73, -12.88) * mm, v(-0.75, -12.88) * mm]});
            skFitSpline(sketch, "E220", {"points": [v(-0.75, -12.88) * mm, v(-0.8, -12.88) * mm, v(-0.87, -12.89) * mm, v(-0.94, -12.94) * mm, v(-0.97, -12.96) * mm]});
            skFitSpline(sketch, "E221", {"points": [v(-0.97, -12.96) * mm, v(-1, -13) * mm, v(-1.05, -13.08) * mm, v(-1.05, -13.18) * mm, v(-1.05, -13.24) * mm]});
            skFitSpline(sketch, "E222", {"points": [v(-1.26, -13.15) * mm, v(-1.26, -13.11) * mm, v(-1.26, -13.04) * mm, v(-1.3, -12.97) * mm, v(-1.31, -12.95) * mm]});
            skFitSpline(sketch, "E223", {"points": [v(-1.31, -12.95) * mm, v(-1.33, -12.93) * mm, v(-1.38, -12.88) * mm, v(-1.44, -12.88) * mm, v(-1.48, -12.88) * mm]});
            skFitSpline(sketch, "E224", {"points": [v(-1.48, -12.88) * mm, v(-1.5, -12.88) * mm, v(-1.56, -12.88) * mm, v(-1.61, -12.9) * mm, v(-1.64, -12.92) * mm]});
            skFitSpline(sketch, "E225", {"points": [v(-1.64, -12.92) * mm, v(-1.66, -12.94) * mm, v(-1.71, -12.98) * mm, v(-1.73, -13.03) * mm, v(-1.75, -13.06) * mm]});
            skFitSpline(sketch, "E226", {"points": [v(-1.75, -13.06) * mm, v(-1.76, -13.1) * mm, v(-1.78, -13.18) * mm, v(-1.78, -13.26) * mm, v(-1.78, -13.31) * mm]});
            skFitSpline(sketch, "E227", {"points": [v(0.16, -12.9) * mm, v(0.19, -12.87) * mm, v(0.23, -12.81) * mm, v(0.29, -12.77) * mm, v(0.32, -12.75) * mm]});
            skFitSpline(sketch, "E228", {"points": [v(0.32, -12.75) * mm, v(0.35, -12.74) * mm, v(0.42, -12.7) * mm, v(0.5, -12.7) * mm, v(0.54, -12.7) * mm]});
            skFitSpline(sketch, "E229", {"points": [v(0.54, -12.7) * mm, v(0.58, -12.7) * mm, v(0.66, -12.7) * mm, v(0.73, -12.74) * mm, v(0.76, -12.75) * mm]});
            skFitSpline(sketch, "E230", {"points": [v(0.76, -12.75) * mm, v(0.79, -12.77) * mm, v(0.84, -12.82) * mm, v(0.87, -12.88) * mm, v(0.88, -12.91) * mm]});
            skFitSpline(sketch, "E231", {"points": [v(0.88, -12.91) * mm, v(0.93, -12.85) * mm, v(1.03, -12.73) * mm, v(1.19, -12.7) * mm, v(1.26, -12.7) * mm]});
            skFitSpline(sketch, "E232", {"points": [v(1.26, -12.7) * mm, v(1.32, -12.7) * mm, v(1.42, -12.7) * mm, v(1.5, -12.77) * mm, v(1.54, -12.8) * mm]});
            skFitSpline(sketch, "E233", {"points": [v(1.54, -12.8) * mm, v(1.57, -12.84) * mm, v(1.63, -12.93) * mm, v(1.64, -13.05) * mm, v(1.64, -13.1) * mm]});
            skFitSpline(sketch, "E234", {"points": [v(1.43, -13.18) * mm, v(1.43, -13.14) * mm, v(1.43, -13.08) * mm, v(1.42, -13.02) * mm, v(1.41, -13) * mm]});
            skFitSpline(sketch, "E235", {"points": [v(1.41, -13) * mm, v(1.4, -12.98) * mm, v(1.39, -12.95) * mm, v(1.36, -12.92) * mm, v(1.34, -12.91) * mm]});
            skFitSpline(sketch, "E236", {"points": [v(1.34, -12.91) * mm, v(1.32, -12.9) * mm, v(1.28, -12.88) * mm, v(1.24, -12.88) * mm, v(1.21, -12.88) * mm]});
            skFitSpline(sketch, "E237", {"points": [v(1.21, -12.88) * mm, v(1.17, -12.88) * mm, v(1.1, -12.89) * mm, v(1.03, -12.94) * mm, v(1, -12.96) * mm]});
            skFitSpline(sketch, "E238", {"points": [v(1, -12.96) * mm, v(0.98, -13) * mm, v(0.92, -13.08) * mm, v(0.92, -13.18) * mm, v(0.91, -13.24) * mm]});
            skFitSpline(sketch, "E239", {"points": [v(0.7, -13.15) * mm, v(0.7, -13.11) * mm, v(0.7, -13.04) * mm, v(0.67, -12.97) * mm, v(0.66, -12.95) * mm]});
            skFitSpline(sketch, "E240", {"points": [v(0.66, -12.95) * mm, v(0.64, -12.93) * mm, v(0.59, -12.88) * mm, v(0.53, -12.88) * mm, v(0.5, -12.88) * mm]});
            skFitSpline(sketch, "E241", {"points": [v(0.5, -12.88) * mm, v(0.46, -12.88) * mm, v(0.4, -12.88) * mm, v(0.35, -12.9) * mm, v(0.33, -12.92) * mm]});
            skFitSpline(sketch, "E242", {"points": [v(0.33, -12.92) * mm, v(0.3, -12.94) * mm, v(0.26, -12.98) * mm, v(0.23, -13.03) * mm, v(0.22, -13.06) * mm]});
            skFitSpline(sketch, "E243", {"points": [v(0.22, -13.06) * mm, v(0.21, -13.1) * mm, v(0.19, -13.18) * mm, v(0.19, -13.26) * mm, v(0.19, -13.31) * mm]});
            skSolve(sketch);
        }
        {
            var Q0;
            Q0 = qSketchRegion(id + "F5", true);
            extrude(context, id + "F6", {"entities" : qUnion([Q0]), "operationType" : NewBodyOperationType.REMOVE, "oppositeDirection" : true, "depth" : 28.3 * mm, "offsetDistance" : 25 * mm});
        }
        {
            var Q0;
            Q0=makeQuery(id+"F1.opRevolve","SWEPT_FACE",FACE,{"disambiguationData":[OSD([sQuery(id+"F0.wireOp",EDGE,"E2")])]});
            cPlane(context, id + "F7", {"entities" : qUnion([Q0]), "cplaneType" : CPlaneType.OFFSET, "offset" : 0.3 * mm, "oppositeDirection" : true, "width" : 150 * mm, "height" : 150 * mm});
        }
        {
            var Q0;
            Q0=qCreatedBy(id+"F7.planeOp",FACE);
            var sketch = newSketch(context, id + "F8", { "sketchPlane" : qUnion([Q0])});
            skLineSegment(sketch, "E244", {"start": v(-3.93, 2.44) * mm, "end": v(-3.93, 5.38) * mm});
            skLineSegment(sketch, "E245", {"start": v(-3.93, 5.38) * mm, "end": v(-1.22, 5.77) * mm});
            skLineSegment(sketch, "E246", {"start": v(-1.22, 5.77) * mm, "end": v(-1.16, 6.14) * mm});
            skLineSegment(sketch, "E247", {"start": v(-1.16, 6.14) * mm, "end": v(-0.52, 7.83) * mm});
            skLineSegment(sketch, "E248", {"start": v(-0.52, 7.83) * mm, "end": v(-0.07, 8.52) * mm});
            skLineSegment(sketch, "E249", {"start": v(-0.07, 8.52) * mm, "end": v(-1.71, 10.72) * mm});
            skLineSegment(sketch, "E250", {"start": v(-1.71, 10.72) * mm, "end": v(0.37, 12.8) * mm});
            skLineSegment(sketch, "E251", {"start": v(0.37, 12.8) * mm, "end": v(2.57, 11.16) * mm});
            skLineSegment(sketch, "E252", {"start": v(2.57, 11.16) * mm, "end": v(3.26, 11.6) * mm});
            skLineSegment(sketch, "E253", {"start": v(3.26, 11.6) * mm, "end": v(4.94, 12.25) * mm});
            skLineSegment(sketch, "E254", {"start": v(4.94, 12.25) * mm, "end": v(5.32, 12.31) * mm});
            skLineSegment(sketch, "E255", {"start": v(5.32, 12.31) * mm, "end": v(5.7, 15.01) * mm});
            skLineSegment(sketch, "E256", {"start": v(5.7, 15.01) * mm, "end": v(8.65, 15.01) * mm});
            skLineSegment(sketch, "E257", {"start": v(8.65, 15.01) * mm, "end": v(9.04, 12.3) * mm});
            skLineSegment(sketch, "E258", {"start": v(9.04, 12.3) * mm, "end": v(10.28, 11.97) * mm});
            skLineSegment(sketch, "E259", {"start": v(10.28, 11.97) * mm, "end": v(11.83, 11.18) * mm});
            skLineSegment(sketch, "E260", {"start": v(11.83, 11.18) * mm, "end": v(14, 12.8) * mm});
            skLineSegment(sketch, "E261", {"start": v(14, 12.8) * mm, "end": v(16.07, 10.72) * mm});
            skLineSegment(sketch, "E262", {"start": v(16.07, 10.72) * mm, "end": v(14.45, 8.56) * mm});
            skLineSegment(sketch, "E263", {"start": v(14.45, 8.56) * mm, "end": v(15.24, 7) * mm});
            skLineSegment(sketch, "E264", {"start": v(15.24, 7) * mm, "end": v(15.57, 5.77) * mm});
            skLineSegment(sketch, "E265", {"start": v(15.57, 5.77) * mm, "end": v(18.29, 5.38) * mm});
            skLineSegment(sketch, "E266", {"start": v(18.29, 5.38) * mm, "end": v(18.29, 2.44) * mm});
            skLineSegment(sketch, "E267", {"start": v(18.29, 2.44) * mm, "end": v(15.58, 2.05) * mm});
            skLineSegment(sketch, "E268", {"start": v(15.58, 2.05) * mm, "end": v(15.52, 1.67) * mm});
            skLineSegment(sketch, "E269", {"start": v(15.52, 1.67) * mm, "end": v(14.88, -0.01) * mm});
            skLineSegment(sketch, "E270", {"start": v(14.88, -0.01) * mm, "end": v(14.43, -0.7) * mm});
            skLineSegment(sketch, "E271", {"start": v(14.43, -0.7) * mm, "end": v(16.07, -2.9) * mm});
            skLineSegment(sketch, "E272", {"start": v(16.07, -2.9) * mm, "end": v(14, -4.99) * mm});
            skLineSegment(sketch, "E273", {"start": v(14, -4.99) * mm, "end": v(11.8, -3.34) * mm});
            skLineSegment(sketch, "E274", {"start": v(11.8, -3.34) * mm, "end": v(11.1, -3.79) * mm});
            skLineSegment(sketch, "E275", {"start": v(11.1, -3.79) * mm, "end": v(10.82, -3.9) * mm});
            skLineSegment(sketch, "E276", {"start": v(10.82, -3.9) * mm, "end": v(8.48, 1.12) * mm});
            skLineSegment(sketch, "E277", {"start": v(8.48, 1.12) * mm, "end": v(8.58, 1.16) * mm});
            skLineSegment(sketch, "E278", {"start": v(8.58, 1.16) * mm, "end": v(9.12, 1.51) * mm});
            skLineSegment(sketch, "E279", {"start": v(9.12, 1.51) * mm, "end": v(9.58, 1.97) * mm});
            skLineSegment(sketch, "E280", {"start": v(9.58, 1.97) * mm, "end": v(9.93, 2.5) * mm});
            skLineSegment(sketch, "E281", {"start": v(9.93, 2.5) * mm, "end": v(10.16, 3.11) * mm});
            skLineSegment(sketch, "E282", {"start": v(10.16, 3.11) * mm, "end": v(10.26, 3.75) * mm});
            skLineSegment(sketch, "E283", {"start": v(10.26, 3.75) * mm, "end": v(10.23, 4.4) * mm});
            skLineSegment(sketch, "E284", {"start": v(10.23, 4.4) * mm, "end": v(10.06, 5.01) * mm});
            skLineSegment(sketch, "E285", {"start": v(10.06, 5.01) * mm, "end": v(9.77, 5.59) * mm});
            skLineSegment(sketch, "E286", {"start": v(9.77, 5.59) * mm, "end": v(9.36, 6.1) * mm});
            skLineSegment(sketch, "E287", {"start": v(9.36, 6.1) * mm, "end": v(8.86, 6.5) * mm});
            skLineSegment(sketch, "E288", {"start": v(8.86, 6.5) * mm, "end": v(8.29, 6.79) * mm});
            skLineSegment(sketch, "E289", {"start": v(8.29, 6.79) * mm, "end": v(7.66, 6.96) * mm});
            skLineSegment(sketch, "E290", {"start": v(7.66, 6.96) * mm, "end": v(7.02, 6.99) * mm});
            skLineSegment(sketch, "E291", {"start": v(7.02, 6.99) * mm, "end": v(6.38, 6.89) * mm});
            skLineSegment(sketch, "E292", {"start": v(6.38, 6.89) * mm, "end": v(5.78, 6.66) * mm});
            skLineSegment(sketch, "E293", {"start": v(5.78, 6.66) * mm, "end": v(5.24, 6.3) * mm});
            skLineSegment(sketch, "E294", {"start": v(5.24, 6.3) * mm, "end": v(4.78, 5.85) * mm});
            skLineSegment(sketch, "E295", {"start": v(4.78, 5.85) * mm, "end": v(4.43, 5.3) * mm});
            skLineSegment(sketch, "E296", {"start": v(4.43, 5.3) * mm, "end": v(4.2, 4.7) * mm});
            skLineSegment(sketch, "E297", {"start": v(4.2, 4.7) * mm, "end": v(4.1, 4.07) * mm});
            skLineSegment(sketch, "E298", {"start": v(4.1, 4.07) * mm, "end": v(4.13, 3.43) * mm});
            skLineSegment(sketch, "E299", {"start": v(4.13, 3.43) * mm, "end": v(4.3, 2.8) * mm});
            skLineSegment(sketch, "E300", {"start": v(4.3, 2.8) * mm, "end": v(4.6, 2.23) * mm});
            skLineSegment(sketch, "E301", {"start": v(4.6, 2.23) * mm, "end": v(5, 1.73) * mm});
            skLineSegment(sketch, "E302", {"start": v(5, 1.73) * mm, "end": v(5.5, 1.32) * mm});
            skLineSegment(sketch, "E303", {"start": v(5.5, 1.32) * mm, "end": v(5.88, 1.13) * mm});
            skLineSegment(sketch, "E304", {"start": v(5.88, 1.13) * mm, "end": v(3.55, -3.88) * mm});
            skLineSegment(sketch, "E305", {"start": v(3.55, -3.88) * mm, "end": v(2.53, -3.36) * mm});
            skLineSegment(sketch, "E306", {"start": v(2.53, -3.36) * mm, "end": v(0.37, -4.99) * mm});
            skLineSegment(sketch, "E307", {"start": v(0.37, -4.99) * mm, "end": v(-1.71, -2.9) * mm});
            skLineSegment(sketch, "E308", {"start": v(-1.71, -2.9) * mm, "end": v(-0.1, -0.74) * mm});
            skLineSegment(sketch, "E309", {"start": v(-0.1, -0.74) * mm, "end": v(-0.88, 0.81) * mm});
            skLineSegment(sketch, "E310", {"start": v(-0.88, 0.81) * mm, "end": v(-1.21, 2.05) * mm});
            skLineSegment(sketch, "E311", {"start": v(-1.21, 2.05) * mm, "end": v(-3.93, 2.44) * mm});
            skSolve(sketch);
        }
        {
            var Q0;
            Q0=makeQuery(id+"F8.imprint","IMPRINT",FACE,{"disambiguationData":[TD([[makeQuery(id+"F8.imprint","IMPRINT",EDGE,{"derivedFrom":sQuery(id+"F8.wireOp",EDGE,"E244")}),-1.0]])]});
            extrude(context, id + "F9", {"entities" : qUnion([Q0]), "operationType" : NewBodyOperationType.ADD, "endBound" : BoundingType.UP_TO_NEXT, "oppositeDirection" : true, "depth" : 4.7 * mm, "offsetDistance" : 25 * mm});
        }
    });
